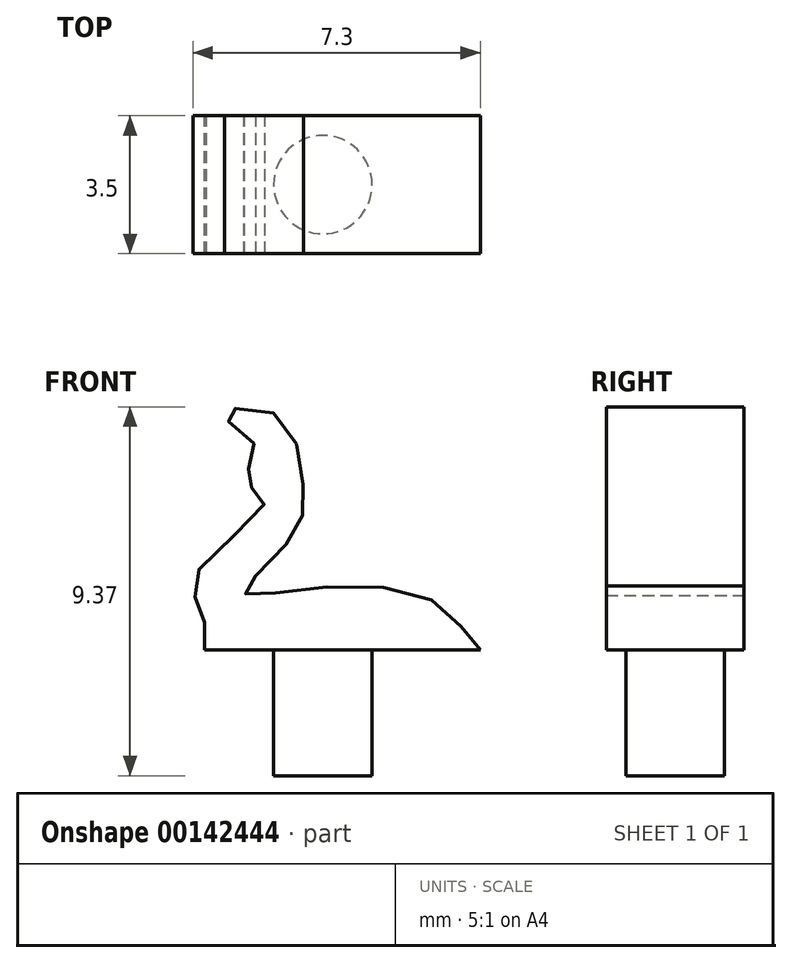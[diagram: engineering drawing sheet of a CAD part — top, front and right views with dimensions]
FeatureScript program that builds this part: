
annotation { "Feature Type Name" : "Feature", "Feature Type Description" : "" }
export const myFeature = defineFeature(function(context is Context, id is Id, definition is map)
    precondition{}
    {
        {
            var Q0;
            Q0=qCreatedBy(makeId("Front.planeOp"),FACE);
            var sketch = newSketch(context, id + "F0", { "sketchPlane" : qUnion([Q0])});
            skLineSegment(sketch, "E0", {"start": v(0, 0) * mm, "end": v(7, 0) * mm});
            skFitSpline(sketch, "E1", {"points": [v(7, 0) * mm, v(5.88, 1.2) * mm, v(2.18, 1.5) * mm, v(1, 1.48) * mm, v(2.23, 2.89) * mm, v(2.5, 4.08) * mm, v(1.78, 6) * mm, v(0.5, 5.96) * mm, v(1.3, 5.12) * mm, v(1.02, 4.3) * mm, v(1.53, 3.82) * mm, v(-0.2, 1.97) * mm, v(-0.1, 1) * mm, v(0, 0) * mm], "startDerivative": vector(-11.44, 7.56) * mm, "endDerivative": vector(-3.99, -16.9) * mm});
            skSolve(sketch);
        }
        {
            var Q0;
            Q0=makeQuery(id+"F0.imprint","IMPRINT",FACE,{"disambiguationData":[TD([[makeQuery(id+"F0.imprint","IMPRINT",EDGE,{"derivedFrom":sQuery(id+"F0.wireOp",EDGE,"E0")}),1.0]])]});
            extrude(context, id + "F1", {"entities" : qUnion([Q0]), "endBound" : BoundingType.SYMMETRIC, "depth" : 3.5 * mm});
        }
        {
            var Q0;
            Q0=qCreatedBy(makeId("Top.planeOp"),FACE);
            var sketch = newSketch(context, id + "F2", { "sketchPlane" : qUnion([Q0])});
            skCircle(sketch, "E2", {"center": v(3, 0) * mm, "radius": 1.25 * mm});
            skSolve(sketch);
        }
        {
            var Q0;
            Q0=makeQuery(id+"F2.imprint","IMPRINT",FACE,{"disambiguationData":[TD([[makeQuery(id+"F2.imprint","IMPRINT",EDGE,{"derivedFrom":sQuery(id+"F2.wireOp",EDGE,"E2")}),1.0]])]});
            extrude(context, id + "F3", {"entities" : qUnion([Q0]), "operationType" : NewBodyOperationType.ADD, "oppositeDirection" : true, "depth" : 3.2 * mm});
        }
    });
